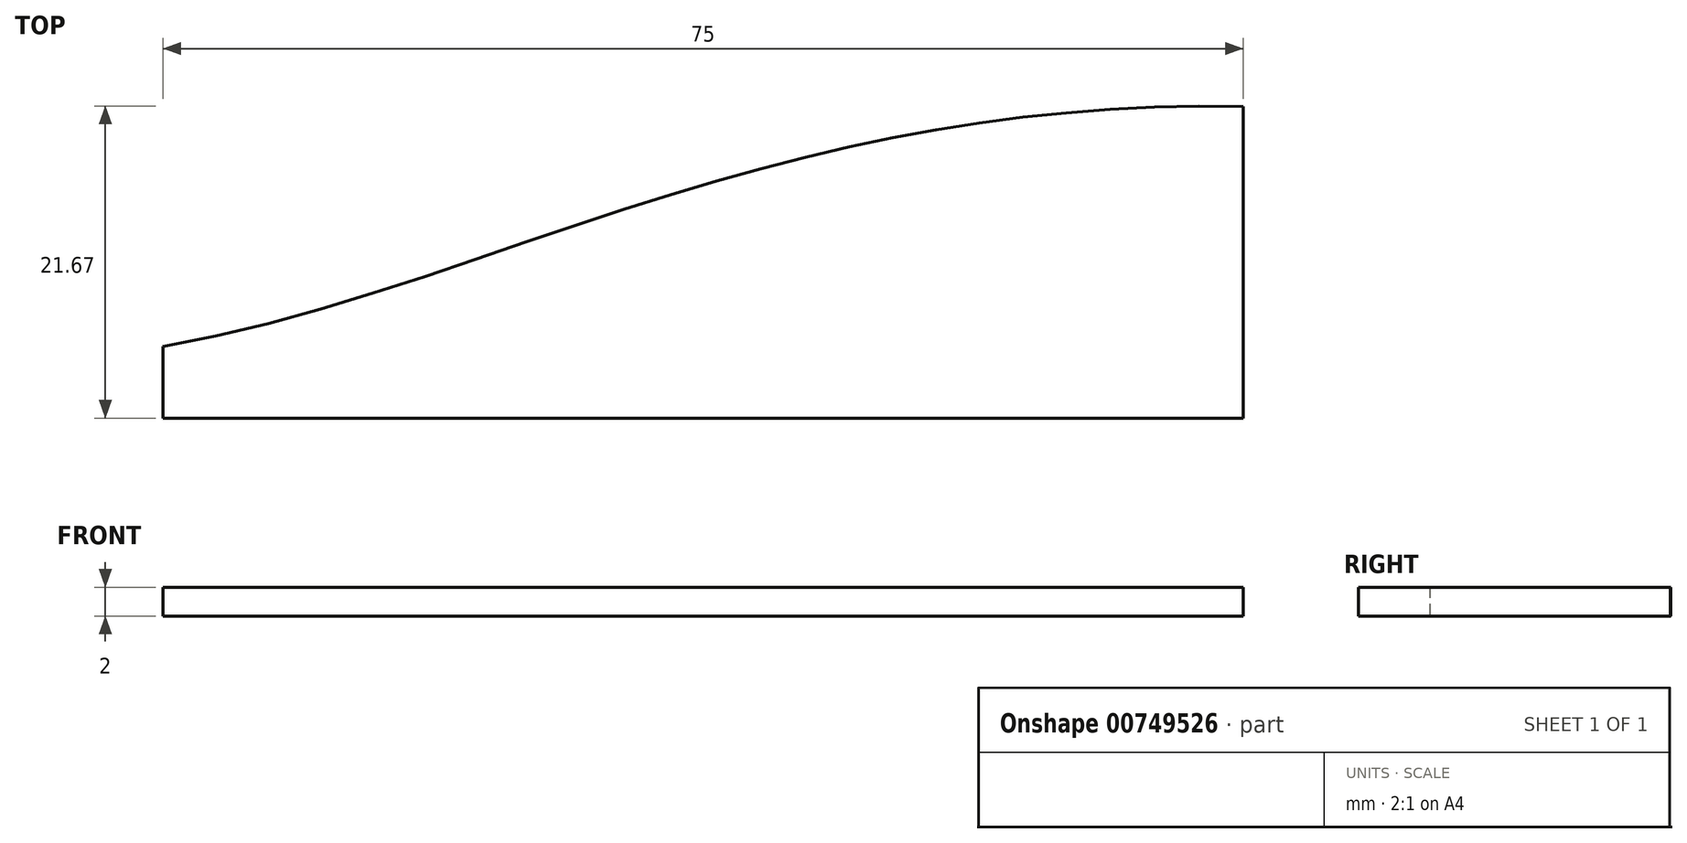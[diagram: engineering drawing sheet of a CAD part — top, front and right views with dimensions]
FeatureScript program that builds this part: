
annotation { "Feature Type Name" : "Feature", "Feature Type Description" : "" }
export const myFeature = defineFeature(function(context is Context, id is Id, definition is map)
    precondition{}
    {
        {
            var Q0;
            Q0=qCreatedBy(makeId("Top.planeOp"),FACE);
            var sketch = newSketch(context, id + "F0", { "sketchPlane" : qUnion([Q0])});
            skLineSegment(sketch, "E0.bottom", {"start": v(37.5, 29) * mm, "end": v(-37.5, 29) * mm});
            skLineSegment(sketch, "E0.top", {"start": v(37.5, -29) * mm, "end": v(-37.5, -29) * mm});
            skLineSegment(sketch, "E0.left", {"start": v(37.5, 29) * mm, "end": v(37.5, -29) * mm});
            skLineSegment(sketch, "E0.right", {"start": v(-37.5, 29) * mm, "end": v(-37.5, -29) * mm});
            skPoint(sketch, "E0.middle", {"position": v(0, 0) * mm});
            skSolve(sketch);
        }
        {
            var Q0;
            Q0 = qSketchRegion(id + "F0", true);
            extrude(context, id + "F1", {"entities" : qUnion([Q0]), "depth" : 2 * mm, "offsetDistance" : 25 * mm});
        }
        {
            var Q0;
            Q0=qCreatedBy(makeId("Top.planeOp"),FACE);
            var sketch = newSketch(context, id + "F2", { "sketchPlane" : qUnion([Q0])});
            skLineSegment(sketch, "E1", {"start": v(-75, 0) * mm, "end": v(74, 0) * mm});
            skLineSegment(sketch, "E2", {"start": v(74, 0) * mm, "end": v(74, 14) * mm});
            skLineSegment(sketch, "E3", {"start": v(-75, 0) * mm, "end": v(-75, 4) * mm});
            skLineSegment(sketch, "E4", {"start": v(-75, 4) * mm, "end": v(-37.37, 4) * mm});
            skFitSpline(sketch, "E5", {"points": [v(74, 14) * mm, v(51.68, 20.34) * mm, v(23.13, 21) * mm, v(-7.03, 14) * mm, v(-47.65, 4) * mm], "startDerivative": vector(-87.92, 32.53) * mm, "endDerivative": vector(-138.48, 0) * mm});
            skSolve(sketch);
        }
        {
            var Q0;
            Q0=makeQuery(id+"F2.imprint","IMPRINT",FACE,{"disambiguationData":[TD([[makeQuery(id+"F2.imprint","IMPRINT",EDGE,{"derivedFrom":sQuery(id+"F2.wireOp",EDGE,"E1")}),1.0]])]});
            extrude(context, id + "F3", {"entities" : qUnion([Q0]), "operationType" : NewBodyOperationType.INTERSECT, "depth" : 2 * mm, "offsetDistance" : 25 * mm});
        }
    });
